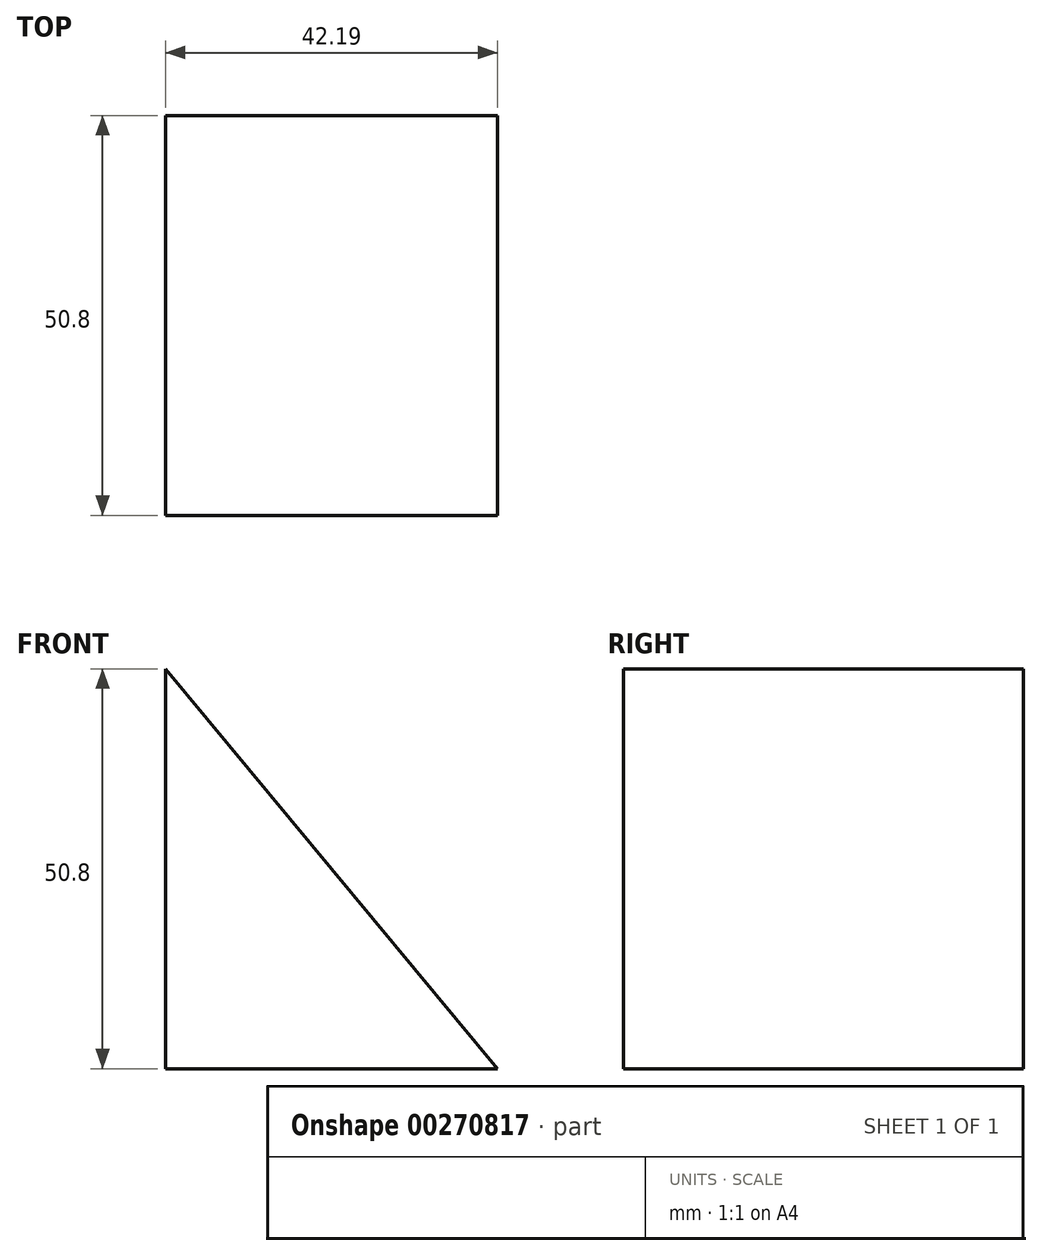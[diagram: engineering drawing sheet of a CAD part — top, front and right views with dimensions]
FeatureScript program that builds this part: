
annotation { "Feature Type Name" : "Feature", "Feature Type Description" : "" }
export const myFeature = defineFeature(function(context is Context, id is Id, definition is map)
    precondition{}
    {
        {
            var Q0;
            Q0=qCreatedBy(makeId("Front.planeOp"),FACE);
            var sketch = newSketch(context, id + "F0", { "sketchPlane" : qUnion([Q0])});
            skLineSegment(sketch, "E0", {"start": v(-59, 0) * mm, "end": v(-59, 50.8) * mm});
            skLineSegment(sketch, "E1", {"start": v(-59, 50.8) * mm, "end": v(-16.8, 0) * mm});
            skLineSegment(sketch, "E2", {"start": v(-16.8, 0) * mm, "end": v(-59, 0) * mm});
            skSolve(sketch);
        }
        {
            var Q0;
            Q0 = qSketchRegion(id + "F0", true);
            extrude(context, id + "F1", {"entities" : qUnion([Q0]), "depth" : 50.8 * mm});
        }
    });
